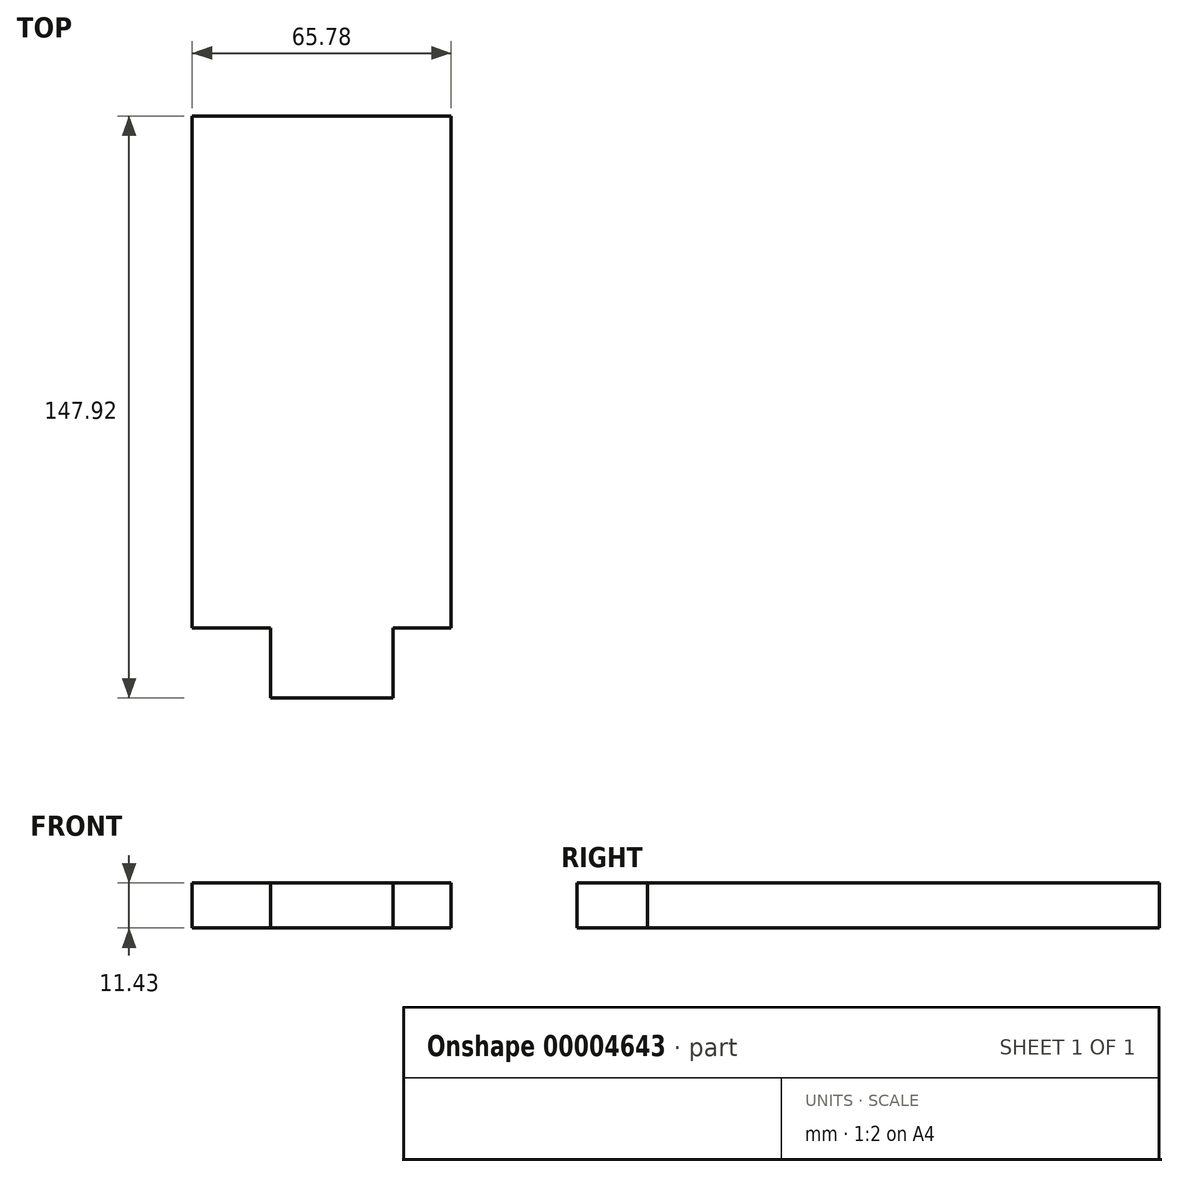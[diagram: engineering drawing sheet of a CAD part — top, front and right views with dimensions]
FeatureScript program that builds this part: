
annotation { "Feature Type Name" : "Feature", "Feature Type Description" : "" }
export const myFeature = defineFeature(function(context is Context, id is Id, definition is map)
    precondition{}
    {
        {
            var Q0;
            Q0=qCreatedBy(makeId("Top.planeOp"),FACE);
            var sketch = newSketch(context, id + "F0", { "sketchPlane" : qUnion([Q0])});
            skLineSegment(sketch, "E0", {"start": v(-35.22, 63.03) * mm, "end": v(-35.22, -67.02) * mm});
            skLineSegment(sketch, "E1", {"start": v(-35.22, -67.02) * mm, "end": v(-15.26, -67.02) * mm});
            skLineSegment(sketch, "E2", {"start": v(30.56, -67.02) * mm, "end": v(30.56, 63.03) * mm});
            skLineSegment(sketch, "E3", {"start": v(30.56, 63.03) * mm, "end": v(-35.22, 63.03) * mm});
            skLineSegment(sketch, "E4", {"start": v(-15.26, -67.02) * mm, "end": v(-15.26, -84.89) * mm});
            skLineSegment(sketch, "E5", {"start": v(-15.26, -84.89) * mm, "end": v(15.86, -84.89) * mm});
            skLineSegment(sketch, "E6", {"start": v(15.86, -84.89) * mm, "end": v(15.86, -67.02) * mm});
            skLineSegment(sketch, "E7.trimOffspring", {"start": v(15.86, -67.02) * mm, "end": v(30.56, -67.02) * mm});
            skSolve(sketch);
        }
        {
            var Q0;
            Q0=makeQuery(id+"F0.imprint","IMPRINT",FACE,{"disambiguationData":[TD([[makeQuery(id+"F0.imprint","IMPRINT",EDGE,{"derivedFrom":sQuery(id+"F0.wireOp",EDGE,"E0")}),1.0]])]});
            extrude(context, id + "F1", {"entities" : qUnion([Q0]), "depth" : 11.43 * mm});
        }
    });
